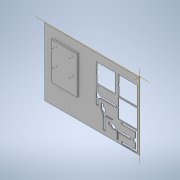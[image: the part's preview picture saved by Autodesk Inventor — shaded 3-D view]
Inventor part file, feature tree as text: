
AUTODESK INVENTOR PART (.ipt)
format: ipt  version: 2022 (Build 260153000, 153)  size: 294,912 bytes
history: native  units: mm
features: extrude x3, sketch x2
ambient origin geometry x8: Origin, YZ Plane, XZ Plane, XY Plane, X Axis, Y Axis, Z Axis, Center Point
bodies: Body1 (feature_tree)
feature tree (5):
  extrude  "Extrusión2"  Depth=500.0mm
  extrude  "Extrusión3"  Depth=700.0mm
  extrude  "Extrusión4"  Depth=60.0mm
  sketch  "Boceto3"  dims[d10=700.0mm d11=500.0mm]
  sketch  "Boceto4"  dims[d12=5.0mm d13=0.0mm d14=700.0mm d15=500.0mm d16=60.0mm d18=150.0mm d19=9.0mm d20=0.0mm d21=5.0mm d22=25.0mm d23=0.0mm]
